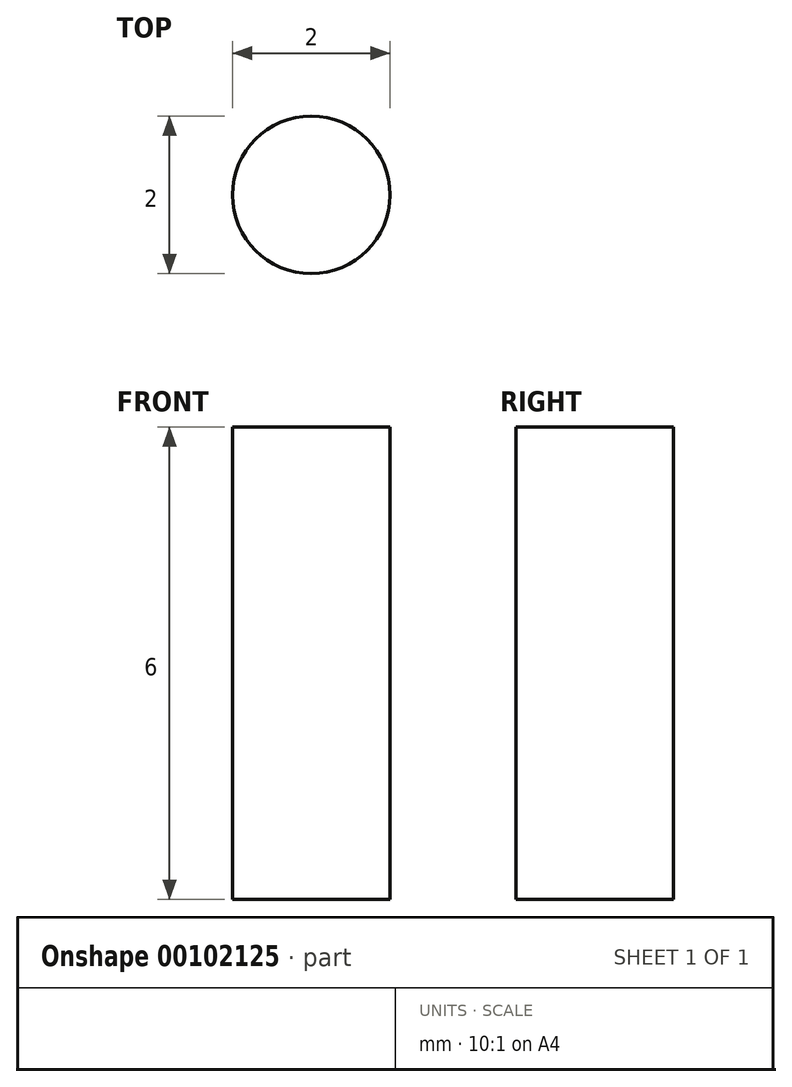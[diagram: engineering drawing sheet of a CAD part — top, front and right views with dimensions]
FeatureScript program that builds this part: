
annotation { "Feature Type Name" : "Feature", "Feature Type Description" : "" }
export const myFeature = defineFeature(function(context is Context, id is Id, definition is map)
    precondition{}
    {
        {
            var Q0;
            Q0=qCreatedBy(makeId("Front.planeOp"),FACE);
            var sketch = newSketch(context, id + "F0", { "sketchPlane" : qUnion([Q0])});
            skLineSegment(sketch, "E0.bottom", {"start": v(8, 3) * mm, "end": v(-8, 3) * mm});
            skLineSegment(sketch, "E0.top", {"start": v(8, -3) * mm, "end": v(-8, -3) * mm});
            skLineSegment(sketch, "E0.left", {"start": v(8, 3) * mm, "end": v(8, -3) * mm});
            skLineSegment(sketch, "E0.right", {"start": v(-8, 3) * mm, "end": v(-8, -3) * mm});
            skPoint(sketch, "E0.middle", {"position": v(0, 0) * mm});
            skLineSegment(sketch, "E1.bottom", {"start": v(-4, -3) * mm, "end": v(4, -3) * mm});
            skLineSegment(sketch, "E1.top", {"start": v(-4, -6) * mm, "end": v(4, -6) * mm});
            skLineSegment(sketch, "E1.left", {"start": v(-4, -3) * mm, "end": v(-4, -6) * mm});
            skLineSegment(sketch, "E1.right", {"start": v(4, -3) * mm, "end": v(4, -6) * mm});
            skSolve(sketch);
        }
        {
            var Q0;
            Q0=makeQuery(id+"F0.imprint","IMPRINT",FACE,{"disambiguationData":[TD([[makeQuery(id+"F0.imprint","IMPRINT",EDGE,{"derivedFrom":sQuery(id+"F0.wireOp",EDGE,"E0.bottom")}),1.0]])]});
            var Q1;
            Q1=makeQuery(id+"F0.imprint","IMPRINT",FACE,{"disambiguationData":[TD([[makeQuery(id+"F0.imprint","IMPRINT",EDGE,{"derivedFrom":sQuery(id+"F0.wireOp",EDGE,"E1.bottom")}),-1.0]])]});
            extrude(context, id + "F1", {"entities" : qUnion([Q0, Q1]), "endBound" : BoundingType.SYMMETRIC, "depth" : 5 * mm});
        }
        {
            var Q0;
            Q0=makeQuery(id+"F1.opExtrude","SWEPT_FACE",FACE,{"disambiguationData":[OSD([sQuery(id+"F0.wireOp",EDGE,"E0.bottom")])]});
            var sketch = newSketch(context, id + "F2", { "sketchPlane" : qUnion([Q0])});
            skCircle(sketch, "E2", {"center": v(-5.5, 0) * mm, "radius": 1 * mm});
            skPoint(sketch, "E3", {"position": v(-6.5, 0) * mm});
            skPoint(sketch, "E4", {"position": v(-4.5, 0) * mm});
            skCircle(sketch, "E5.MirrorC", {"center": v(5.5, 0) * mm, "radius": 1 * mm});
            skSolve(sketch);
        }
        {
            var Q0;
            Q0=makeQuery(id+"F2.imprint","IMPRINT",FACE,{"disambiguationData":[TD([[makeQuery(id+"F2.imprint","IMPRINT",EDGE,{"derivedFrom":sQuery(id+"F2.wireOp",EDGE,"E2")}),1.0]])]});
            var Q1;
            Q1=makeQuery(id+"F2.imprint","IMPRINT",FACE,{"disambiguationData":[TD([[makeQuery(id+"F2.imprint","IMPRINT",EDGE,{"derivedFrom":sQuery(id+"F2.wireOp",EDGE,"E5.MirrorC")}),-1.0]])]});
            extrude(context, id + "F3", {"entities" : qUnion([Q0, Q1]), "operationType" : NewBodyOperationType.REMOVE, "endBound" : BoundingType.THROUGH_ALL, "oppositeDirection" : true, "depth" : 25.4 * mm});
        }
    });
